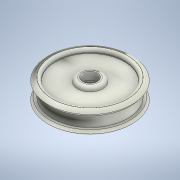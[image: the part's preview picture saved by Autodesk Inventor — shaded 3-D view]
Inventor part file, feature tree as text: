
AUTODESK INVENTOR PART (.ipt)
format: ipt  version: 2022 (Build 260153000, 153)  size: 226,816 bytes
history: native  units: mm
features: extrude x7, sketch x7, fillet x3, chamfer x1
ambient origin geometry x8: Origin, YZ Plane, XZ Plane, XY Plane, X Axis, Y Axis, Z Axis, Center Point
bodies: Solid1 (feature_tree)
feature tree (18):
  extrude  "Extrusion1"  Depth=2.0mm TaperAngle=0.0deg
  extrude  "Extrusion2"  Depth=4.8mm TaperAngle=0.0deg
  extrude  "Extrusion3"  Depth=2.0mm
  fillet  "Fillet1"  Radius=27.5mm
  chamfer  "Chamfer1"  Distance=1.5mm
  extrude  "Extrusion4"  Depth=1.5mm
  fillet  "Fillet2"  Radius=6.0mm
  fillet  "Fillet3"  Radius=3.2mm
  extrude  "Extrusion5"  Depth=5.0mm TaperAngle=0.0deg
  extrude  "Extrusion6"  Depth=5.0mm TaperAngle=0.0deg
  extrude  "Extrusion7"  Depth=5.0mm
  sketch  "Sketch1"  dims[d0=17.0mm d1=2.0mm d2=0.0mm]
  sketch  "Sketch2"  dims[d3=15.0mm d4=4.8mm d5=0.0mm]
  sketch  "Sketch3"  dims[d6=2.0mm d7=0.0mm d8=2.0mm]
  sketch  "Sketch4"  dims[d9=1.0mm d10=2.0mm d11=45.0deg d12=27.5mm]
  sketch  "Sketch5"  dims[d13=10.0mm d14=1.5mm d15=0.0mm]
  sketch  "Sketch6"  dims[d16=1.2mm d17=1.5mm d18=6.0mm d19=3.2mm d20=0.0mm]
  sketch  "Sketch7"  dims[d21=4.0mm d22=5.0mm d23=0.0mm d24=5.0mm d25=0.0mm d26=0.2mm]
